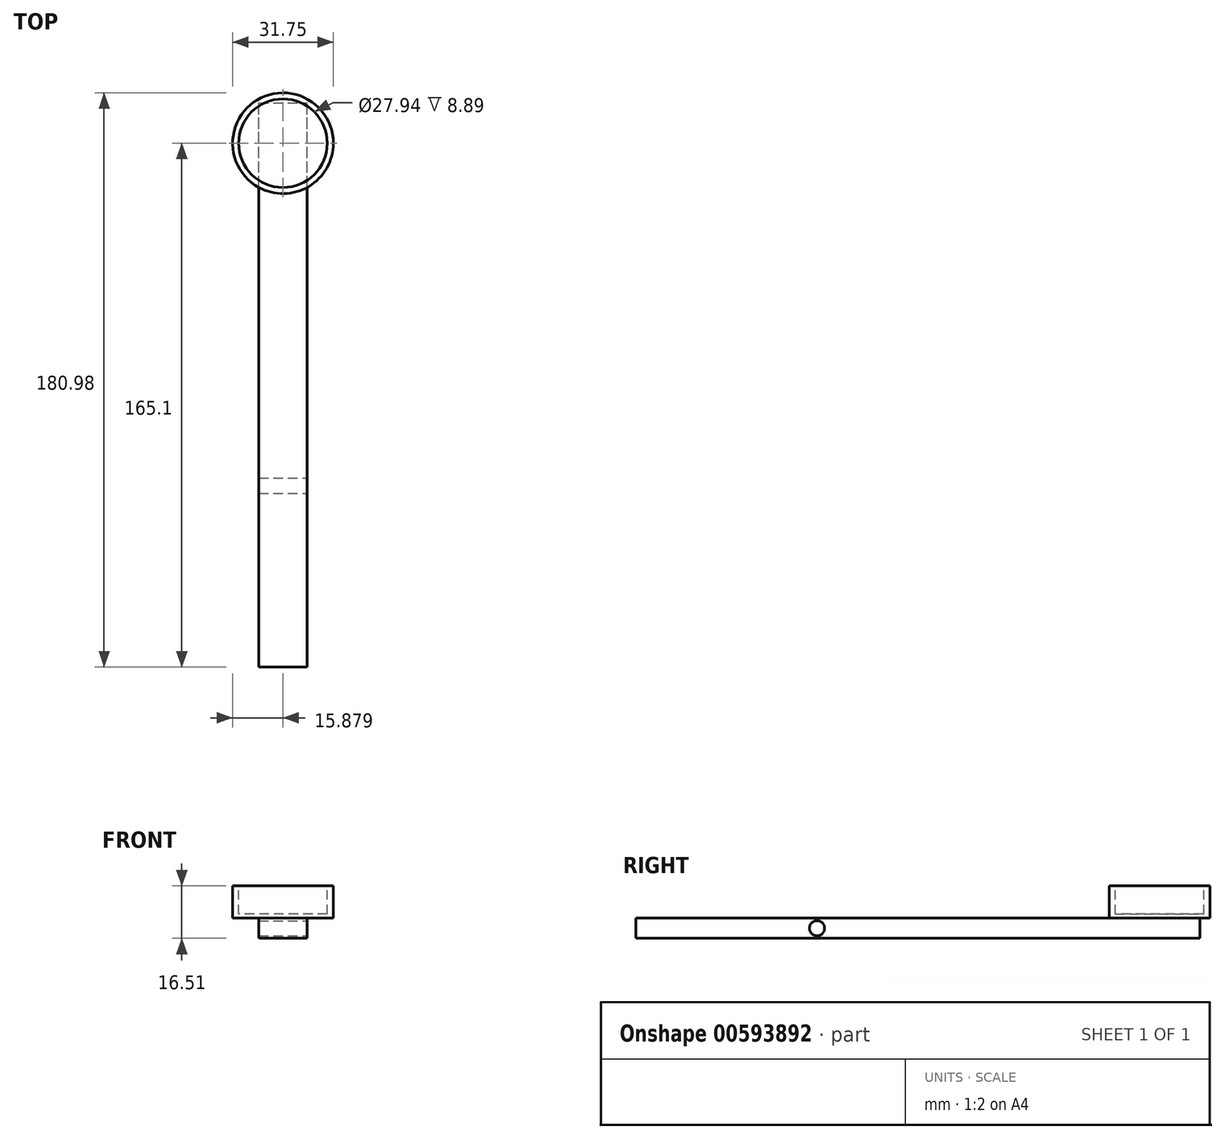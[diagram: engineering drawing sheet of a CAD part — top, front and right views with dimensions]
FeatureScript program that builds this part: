
annotation { "Feature Type Name" : "Feature", "Feature Type Description" : "" }
export const myFeature = defineFeature(function(context is Context, id is Id, definition is map)
    precondition{}
    {
        {
            var Q0;
            Q0=qCreatedBy(makeId("Front.planeOp"),FACE);
            var sketch = newSketch(context, id + "F0", { "sketchPlane" : qUnion([Q0])});
            skLineSegment(sketch, "E0.bottom", {"start": v(-6.42, 6.35) * mm, "end": v(8.82, 6.35) * mm});
            skLineSegment(sketch, "E0.top", {"start": v(-6.42, 0) * mm, "end": v(8.82, 0) * mm});
            skLineSegment(sketch, "E0.left", {"start": v(-6.42, 6.35) * mm, "end": v(-6.42, 0) * mm});
            skLineSegment(sketch, "E0.right", {"start": v(8.82, 6.35) * mm, "end": v(8.82, 0) * mm});
            skSolve(sketch);
        }
        {
            var Q0;
            Q0 = qSketchRegion(id + "F0", true);
            extrude(context, id + "F1", {"entities" : qUnion([Q0]), "depth" : 177.8 * mm, "offsetDistance" : 25.4 * mm});
        }
        {
            var Q0;
            Q0=makeQuery(id+"F1.opExtrude","SWEPT_FACE",FACE,{"disambiguationData":[OSD([sQuery(id+"F0.wireOp",EDGE,"E0.right")])]});
            var sketch = newSketch(context, id + "F2", { "sketchPlane" : qUnion([Q0])});
            skCircle(sketch, "E1", {"center": v(-120.65, 3.18) * mm, "radius": 2.38 * mm});
            skPoint(sketch, "E2", {"position": v(-177.8, 3.17) * mm});
            skSolve(sketch);
        }
        {
            var Q0;
            Q0 = qSketchRegion(id + "F2", true);
            extrude(context, id + "F3", {"entities" : qUnion([Q0]), "operationType" : NewBodyOperationType.REMOVE, "endBound" : BoundingType.THROUGH_ALL, "oppositeDirection" : true, "depth" : 25.4 * mm, "offsetDistance" : 25.4 * mm});
        }
        {
            var Q0;
            Q0=makeQuery(id+"F1.opExtrude","SWEPT_FACE",FACE,{"disambiguationData":[OSD([sQuery(id+"F0.wireOp",EDGE,"E0.bottom")])]});
            var sketch = newSketch(context, id + "F4", { "sketchPlane" : qUnion([Q0])});
            skCircle(sketch, "E3", {"center": v(1.2, -12.7) * mm, "radius": 15.88 * mm});
            skPoint(sketch, "E3.centerSnap0", {"position": v(1.2, 0) * mm});
            skSolve(sketch);
        }
        {
            var Q0;
            Q0 = qSketchRegion(id + "F4", true);
            extrude(context, id + "F5", {"entities" : qUnion([Q0]), "operationType" : NewBodyOperationType.ADD, "depth" : 10.16 * mm, "offsetDistance" : 25.4 * mm});
        }
        {
            var Q0;
            Q0=makeQuery(id+"F5.opExtrude","CAP_FACE",FACE,{"disambiguationData":[OSD([sQuery(id+"F4.wireOp",EDGE,"E3")])],"isStart":false});
            var sketch = newSketch(context, id + "F6", { "sketchPlane" : qUnion([Q0])});
            skCircle(sketch, "E4", {"center": v(1.2, -12.7) * mm, "radius": 13.97 * mm});
            skSolve(sketch);
        }
        {
            var Q0;
            Q0 = qSketchRegion(id + "F6", true);
            extrude(context, id + "F7", {"entities" : qUnion([Q0]), "operationType" : NewBodyOperationType.REMOVE, "oppositeDirection" : true, "depth" : 8.9 * mm, "offsetDistance" : 25.4 * mm});
        }
    });
